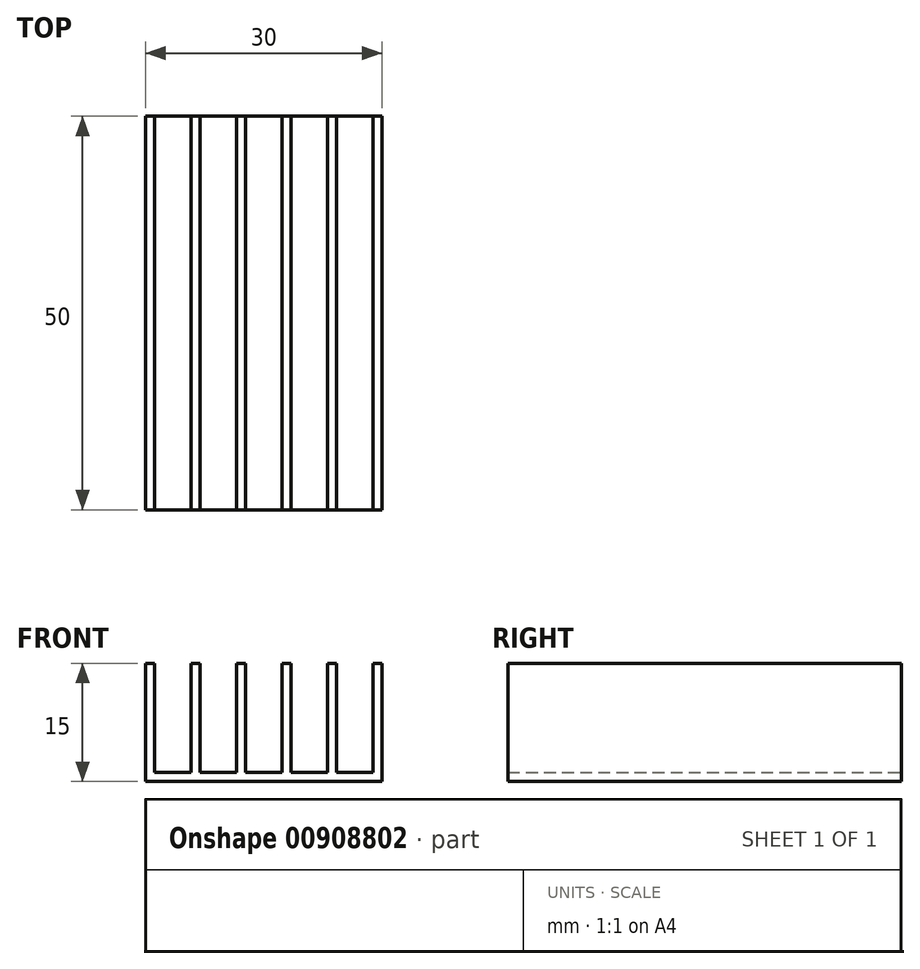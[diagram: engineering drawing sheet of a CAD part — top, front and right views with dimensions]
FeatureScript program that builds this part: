
annotation { "Feature Type Name" : "Feature", "Feature Type Description" : "" }
export const myFeature = defineFeature(function(context is Context, id is Id, definition is map)
    precondition{}
    {
        {
            var Q0;
            Q0=qCreatedBy(makeId("Front.planeOp"),FACE);
            var sketch = newSketch(context, id + "F0", { "sketchPlane" : qUnion([Q0])});
            skLineSegment(sketch, "E0.bottom", {"start": v(15, -7.5) * mm, "end": v(-15, -7.5) * mm});
            skLineSegment(sketch, "E0.left", {"start": v(15, -7.5) * mm, "end": v(15, 7.5) * mm});
            skLineSegment(sketch, "E0.right", {"start": v(-15, -7.5) * mm, "end": v(-15, 7.5) * mm});
            skPoint(sketch, "E0.middle", {"position": v(0, 0) * mm});
            skLineSegment(sketch, "E1", {"start": v(-15, 7.5) * mm, "end": v(-13.88, 7.5) * mm});
            skLineSegment(sketch, "E2", {"start": v(-13.88, 7.5) * mm, "end": v(-13.88, -6.36) * mm});
            skLineSegment(sketch, "E3", {"start": v(-13.88, -6.36) * mm, "end": v(-9.22, -6.36) * mm});
            skLineSegment(sketch, "E4", {"start": v(-9.22, -6.36) * mm, "end": v(-9.22, 7.5) * mm});
            skLineSegment(sketch, "E5", {"start": v(-9.22, 7.5) * mm, "end": v(-8.1, 7.5) * mm});
            skLineSegment(sketch, "E6", {"start": v(-8.1, 7.5) * mm, "end": v(-8.1, -6.36) * mm});
            skLineSegment(sketch, "E7", {"start": v(-8.1, -6.36) * mm, "end": v(-3.45, -6.36) * mm});
            skLineSegment(sketch, "E8", {"start": v(-3.45, -6.36) * mm, "end": v(-3.45, 7.5) * mm});
            skLineSegment(sketch, "E9", {"start": v(-3.45, 7.5) * mm, "end": v(-2.33, 7.5) * mm});
            skLineSegment(sketch, "E10", {"start": v(-2.33, 7.5) * mm, "end": v(-2.33, -6.36) * mm});
            skLineSegment(sketch, "E11", {"start": v(-2.33, -6.36) * mm, "end": v(2.33, -6.36) * mm});
            skLineSegment(sketch, "E12", {"start": v(2.33, -6.36) * mm, "end": v(2.33, 7.5) * mm});
            skLineSegment(sketch, "E13", {"start": v(2.33, 7.5) * mm, "end": v(3.45, 7.5) * mm});
            skLineSegment(sketch, "E14", {"start": v(3.45, 7.5) * mm, "end": v(3.45, -6.36) * mm});
            skLineSegment(sketch, "E15", {"start": v(3.45, -6.36) * mm, "end": v(8.1, -6.36) * mm});
            skLineSegment(sketch, "E16", {"start": v(8.1, -6.36) * mm, "end": v(8.1, 7.5) * mm});
            skLineSegment(sketch, "E17", {"start": v(8.1, 7.5) * mm, "end": v(9.22, 7.5) * mm});
            skLineSegment(sketch, "E18", {"start": v(9.22, 7.5) * mm, "end": v(9.22, -6.36) * mm});
            skLineSegment(sketch, "E19", {"start": v(9.22, -6.36) * mm, "end": v(13.88, -6.36) * mm});
            skLineSegment(sketch, "E20", {"start": v(13.88, -6.36) * mm, "end": v(13.88, 7.5) * mm});
            skLineSegment(sketch, "E21", {"start": v(13.88, 7.5) * mm, "end": v(15, 7.5) * mm});
            skSolve(sketch);
        }
        {
            var Q0;
            Q0 = qSketchRegion(id + "F0", true);
            extrude(context, id + "F1", {"entities" : qUnion([Q0]), "depth" : 50 * mm, "offsetDistance" : 25 * mm});
        }
    });
